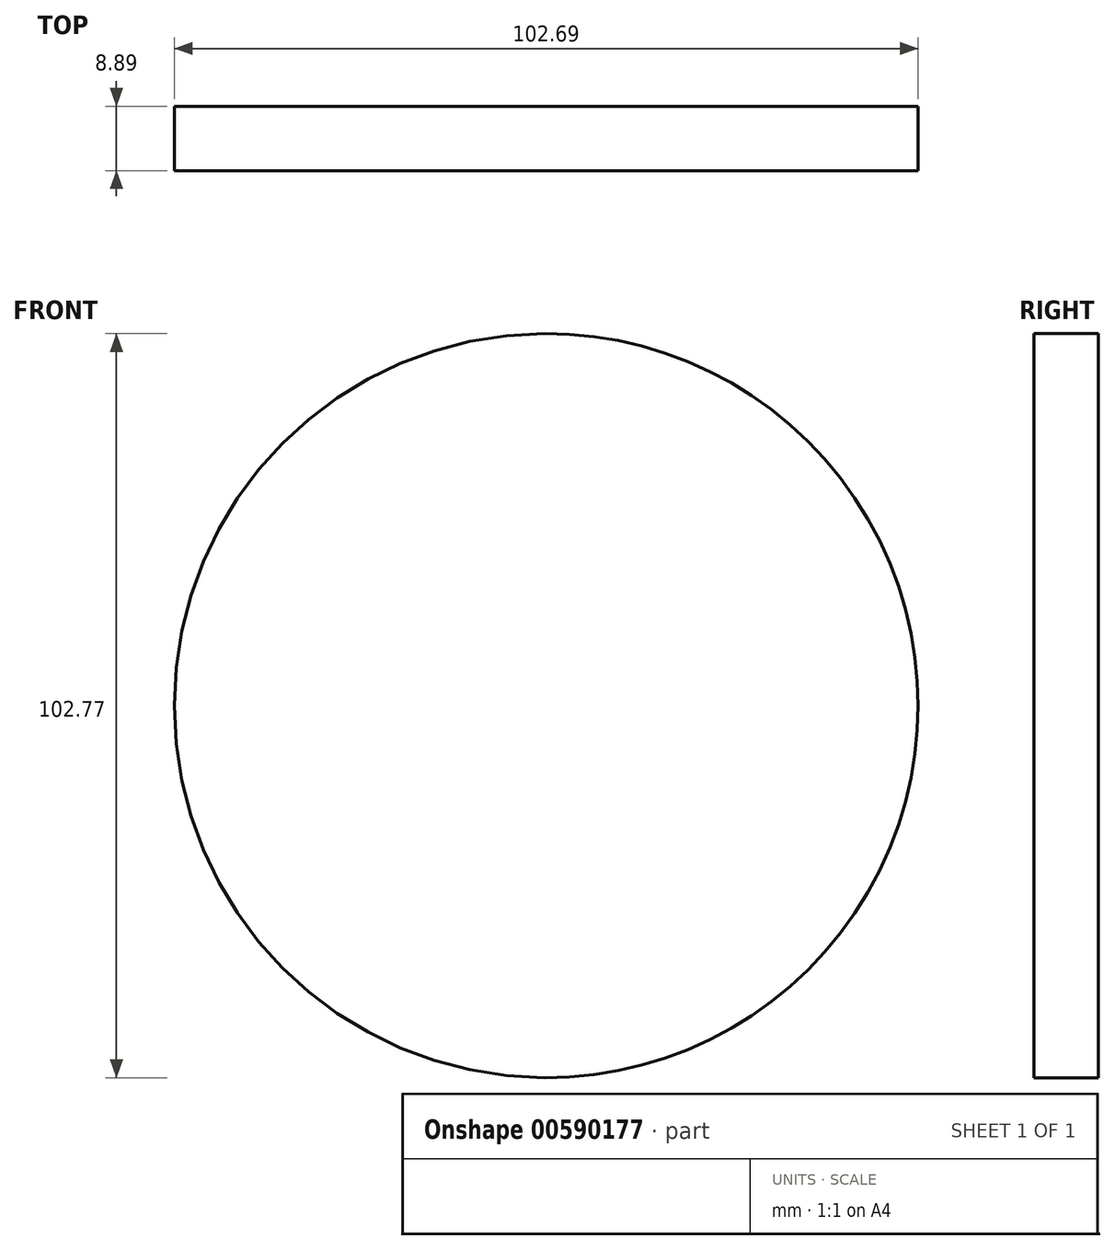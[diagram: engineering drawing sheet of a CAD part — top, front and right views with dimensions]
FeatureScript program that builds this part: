
annotation { "Feature Type Name" : "Feature", "Feature Type Description" : "" }
export const myFeature = defineFeature(function(context is Context, id is Id, definition is map)
    precondition{}
    {
        {
            var Q0;
            Q0=qCreatedBy(makeId("Front.planeOp"),FACE);
            var sketch = newSketch(context, id + "F0", { "sketchPlane" : qUnion([Q0])});
            skArc(sketch, "E0", {"start": v(6.6, -58.28) * mm, "mid": v(58.2, -6.9) * mm, "end": v(6.6, 44.5) * mm});
            skArc(sketch, "E1", {"start": v(6.6, 44.5) * mm, "mid": v(-44.49, -6.9) * mm, "end": v(6.6, -58.28) * mm});
            skSolve(sketch);
        }
        {
            var Q0;
            Q0 = qSketchRegion(id + "F0", true);
            extrude(context, id + "F1", {"entities" : qUnion([Q0]), "depth" : 8.9 * mm, "offsetDistance" : 25.4 * mm});
        }
    });
